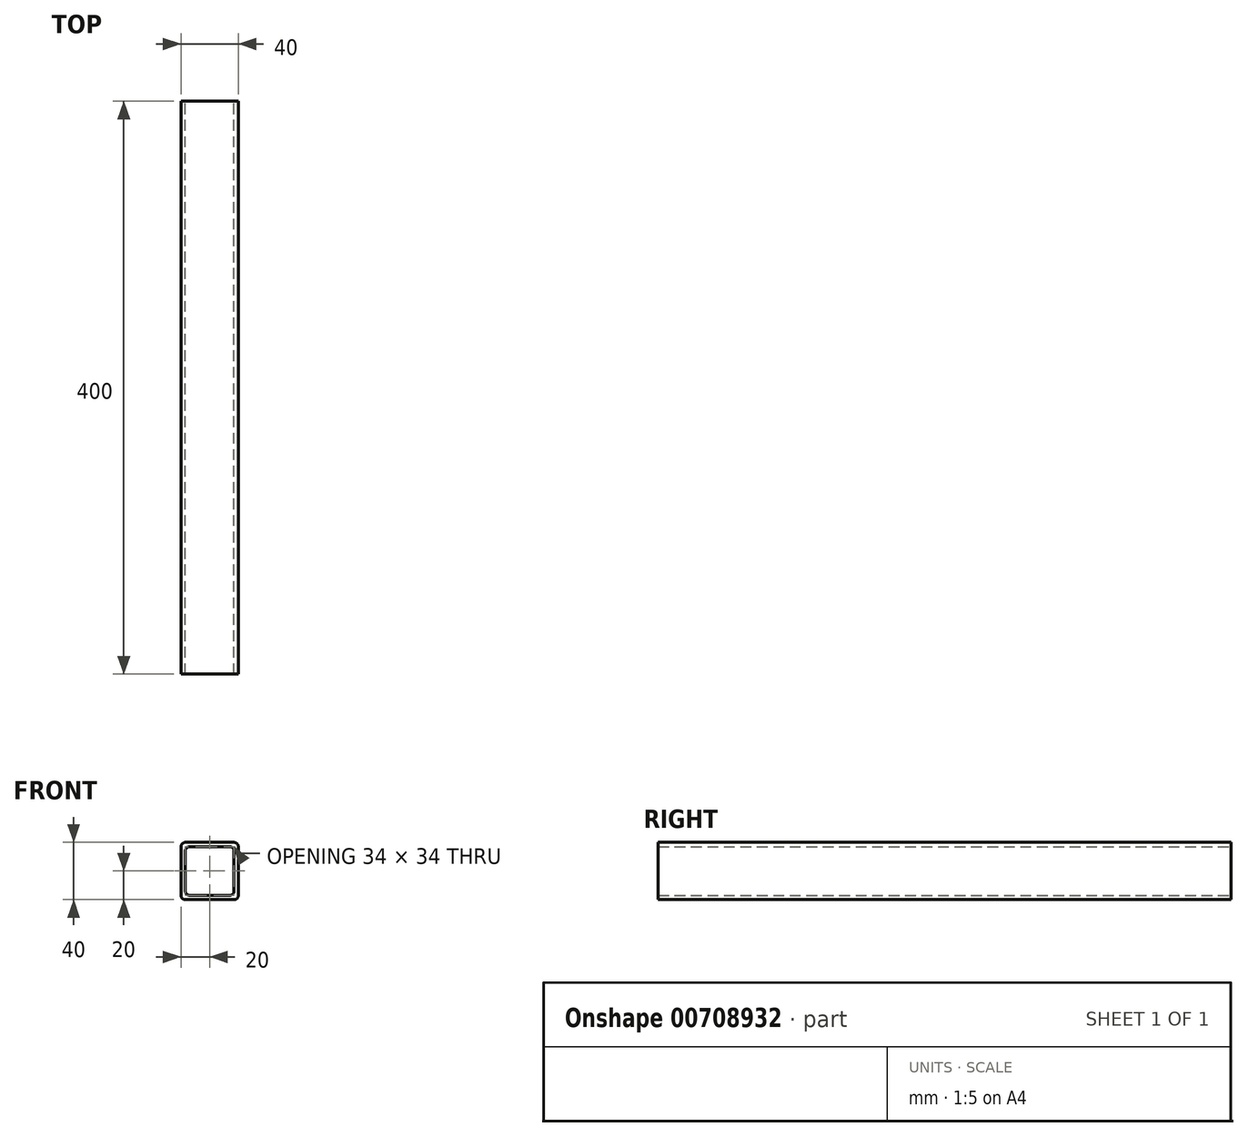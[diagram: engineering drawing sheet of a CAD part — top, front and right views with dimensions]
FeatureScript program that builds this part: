
annotation { "Feature Type Name" : "Feature", "Feature Type Description" : "" }
export const myFeature = defineFeature(function(context is Context, id is Id, definition is map)
    precondition{}
    {
        {
            var Q0;
            Q0=qCreatedBy(makeId("Front.planeOp"),FACE);
            var sketch = newSketch(context, id + "F0", { "sketchPlane" : qUnion([Q0])});
            skLineSegment(sketch, "E0.bottom", {"start": v(17, 20) * mm, "end": v(-17, 20) * mm});
            skLineSegment(sketch, "E0.top", {"start": v(17, -20) * mm, "end": v(-17, -20) * mm});
            skLineSegment(sketch, "E0.left", {"start": v(20, 17) * mm, "end": v(20, -17) * mm});
            skLineSegment(sketch, "E0.right", {"start": v(-20, 17) * mm, "end": v(-20, -17) * mm});
            skPoint(sketch, "E0.middle", {"position": v(0, 0) * mm});
            skLineSegment(sketch, "E1.0", {"start": v(14, 17) * mm, "end": v(-14, 17) * mm});
            skLineSegment(sketch, "E1.1", {"start": v(17, 14) * mm, "end": v(17, -14) * mm});
            skLineSegment(sketch, "E1.2", {"start": v(14, -17) * mm, "end": v(-14, -17) * mm});
            skLineSegment(sketch, "E1.3", {"start": v(-17, 14) * mm, "end": v(-17, -14) * mm});
            skPoint(sketch, "E2.visualSharp", {"position": v(-17, 17) * mm});
            skArc(sketch, "E2.filletArc", {"start": v(-14, 17) * mm, "mid": v(-16.12, 16.12) * mm, "end": v(-17, 14) * mm});
            skPoint(sketch, "E3.visualSharp", {"position": v(17, 17) * mm});
            skArc(sketch, "E3.filletArc", {"start": v(17, 14) * mm, "mid": v(16.12, 16.12) * mm, "end": v(14, 17) * mm});
            skPoint(sketch, "E4.visualSharp", {"position": v(17, -17) * mm});
            skArc(sketch, "E4.filletArc", {"start": v(14, -17) * mm, "mid": v(16.12, -16.12) * mm, "end": v(17, -14) * mm});
            skPoint(sketch, "E5.visualSharp", {"position": v(-17, -17) * mm});
            skArc(sketch, "E5.filletArc", {"start": v(-17, -14) * mm, "mid": v(-16.12, -16.12) * mm, "end": v(-14, -17) * mm});
            skPoint(sketch, "E6.visualSharp", {"position": v(-20, -20) * mm});
            skArc(sketch, "E6.filletArc", {"start": v(-20, -17) * mm, "mid": v(-19.12, -19.12) * mm, "end": v(-17, -20) * mm});
            skPoint(sketch, "E7.visualSharp", {"position": v(20, -20) * mm});
            skArc(sketch, "E7.filletArc", {"start": v(17, -20) * mm, "mid": v(19.12, -19.12) * mm, "end": v(20, -17) * mm});
            skPoint(sketch, "E8.visualSharp", {"position": v(-20, 20) * mm});
            skArc(sketch, "E8.filletArc", {"start": v(-17, 20) * mm, "mid": v(-19.12, 19.12) * mm, "end": v(-20, 17) * mm});
            skPoint(sketch, "E9.visualSharp", {"position": v(20, 20) * mm});
            skArc(sketch, "E9.filletArc", {"start": v(20, 17) * mm, "mid": v(19.12, 19.12) * mm, "end": v(17, 20) * mm});
            skSolve(sketch);
        }
        {
            var Q0;
            Q0=makeQuery(id+"F0.imprint","IMPRINT",FACE,{"disambiguationData":[TD([[makeQuery(id+"F0.imprint","IMPRINT",EDGE,{"derivedFrom":sQuery(id+"F0.wireOp",EDGE,"E0.bottom")}),1.0]])]});
            extrude(context, id + "F1", {"entities" : qUnion([Q0]), "endBound" : BoundingType.SYMMETRIC, "depth" : 400 * mm, "offsetDistance" : 25 * mm});
        }
    });
